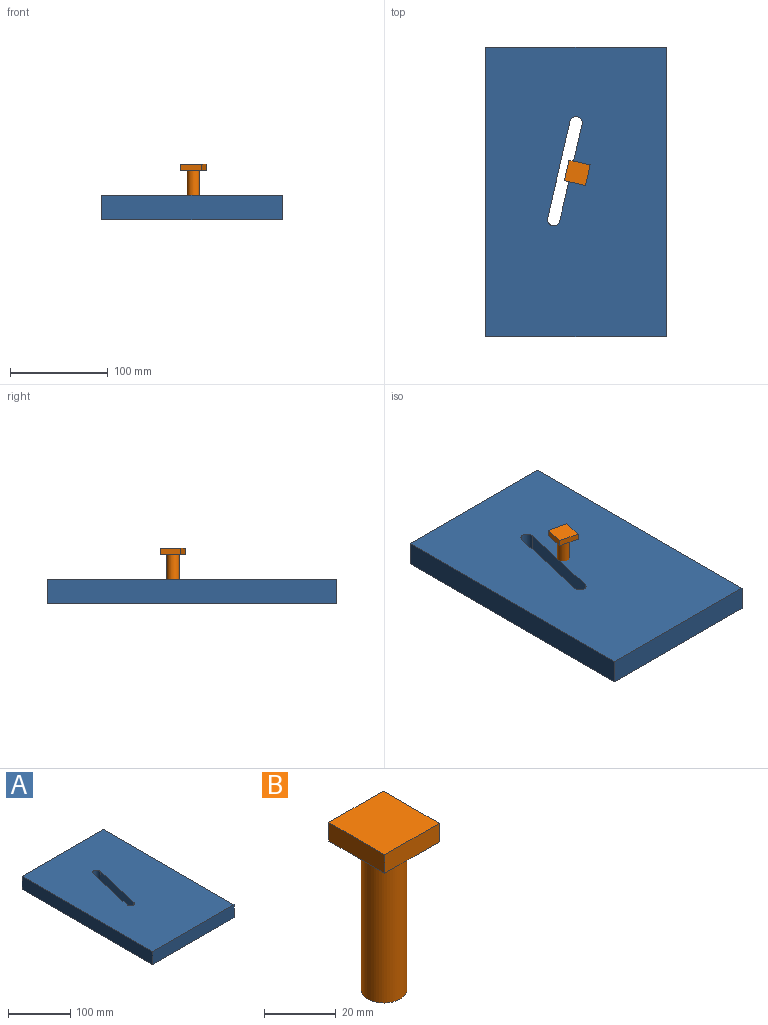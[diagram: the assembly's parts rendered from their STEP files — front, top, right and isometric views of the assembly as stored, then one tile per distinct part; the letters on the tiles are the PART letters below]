
ASSEMBLY  parts=2 mates=1
PART A: 10 faces, bbox 184.2x296x25.4 mm
  f0: plane 99.01x25.4mm, normal (-0.97,0.22,0), area 2580.6mm2, adj f1,f7,f8,f9
  f1: cylinder r=6.35mm len=25.4mm, axis (0,0,-1), area 506.7mm2, adj f0,f2,f8,f9
  f2: plane 99.01x25.4mm, normal (0.97,-0.22,0), area 2580.6mm2, adj f1,f7,f8,f9
  f3: plane 184.15x25.4mm, normal (0,1,0), area 4677.4mm2, adj f4,f6,f8,f9
  f4: plane 295.96x25.4mm, normal (-1,0,0), area 7517.4mm2, adj f3,f5,f8,f9
  f5: plane 184.15x25.4mm, normal (0,-1,0), area 4677.4mm2, adj f4,f6,f8,f9
  f6: plane 295.96x25.4mm, normal (1,0,0), area 7517.4mm2, adj f3,f5,f8,f9
  f7: cylinder r=6.35mm len=25.4mm, axis (0,0,-1), area 506.7mm2, adj f0,f2,f8,f9
  f8: plane 295.96x184.15mm, normal (0,0,1), area 53084.3mm2, adj f0,f1,f2,f3,f4,f5,f6,f7
  f9: plane 295.96x184.15mm, normal (0,0,-1), area 53084.3mm2, adj f0,f1,f2,f3,f4,f5,f6,f7
PART B: 8 faces, bbox 21.5x22.1x57.2 mm
  f0: cylinder r=6.35mm len=50.8mm, axis (0,0,-1), area 2026.8mm2, adj f1,f7
  f1: plane 12.7x12.7mm, normal (0,0,-1), area 126.7mm2, adj f0
  f2: plane 21.53x6.35mm, normal (0,1,0), area 136.7mm2, adj f3,f5,f6,f7
  f3: plane 22.12x6.35mm, normal (-1,0,0), area 140.4mm2, adj f2,f4,f6,f7
  f4: plane 21.53x6.35mm, normal (0,-1,0), area 136.7mm2, adj f3,f5,f6,f7
  f5: plane 22.12x6.35mm, normal (1,0,0), area 140.4mm2, adj f2,f4,f6,f7
  f6: plane 22.12x21.53mm, normal (0,0,1), area 476.1mm2, adj f2,f3,f4,f5
  f7: plane 22.12x21.53mm, normal (0,0,-1), area 349.4mm2, adj f0,f2,f3,f4,f5
PLACE A t=(-52.36,-16.61,-4.97)mm fixed
PLACE B rot(axis=(0,0,-1),102.7deg) t=(-101.23,14.22,-4.97)mm
MATE planar B.f0 <-> A.f9  axis (0,0,-1) through (-51.11,2.93,-4.97)mm
